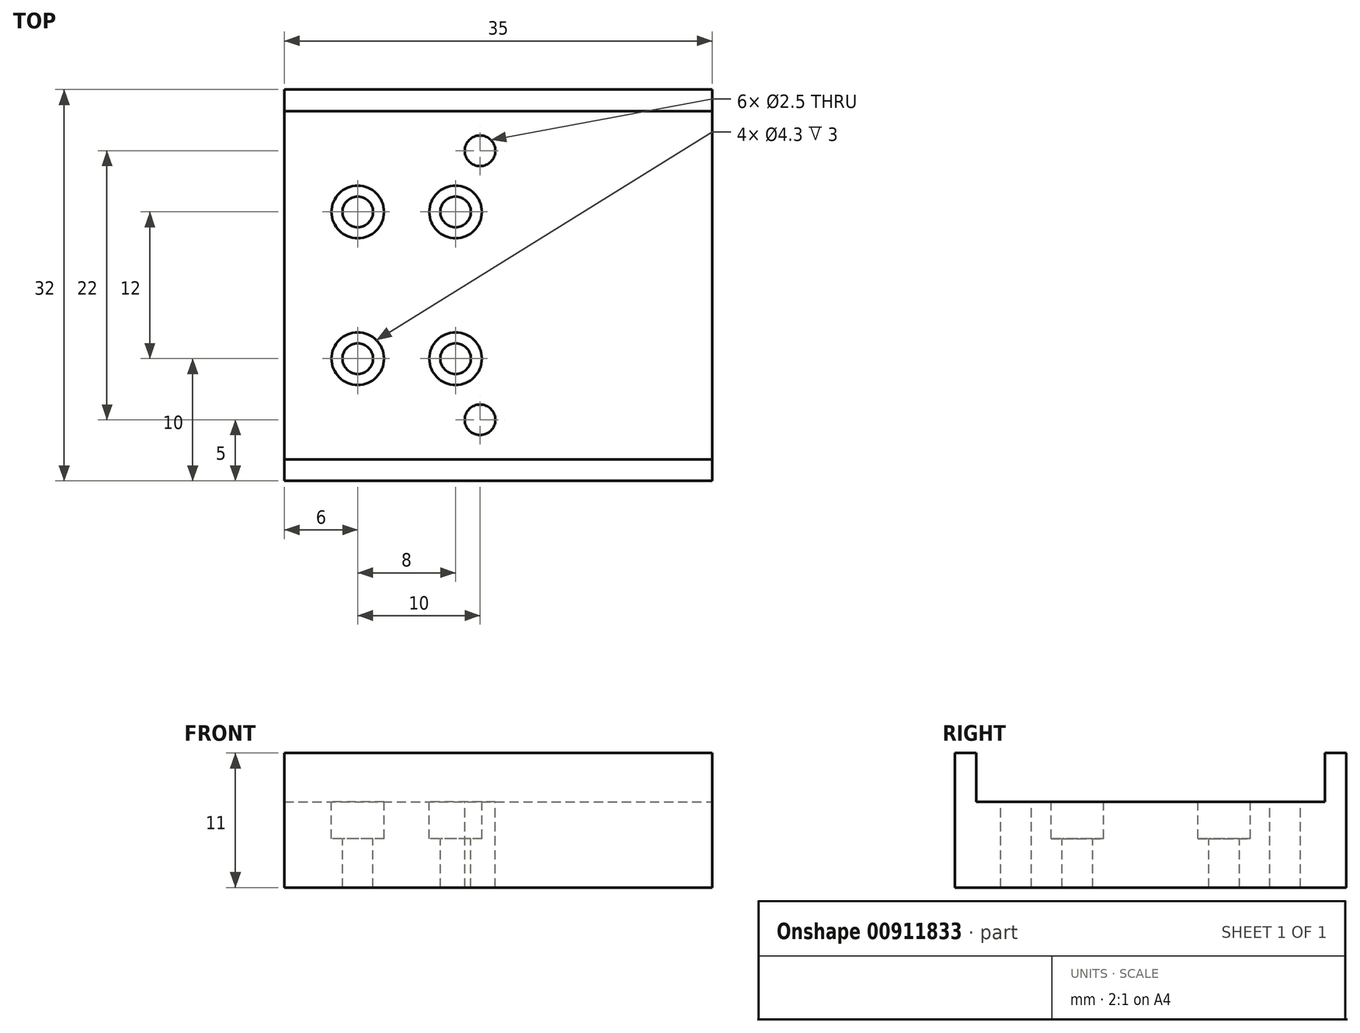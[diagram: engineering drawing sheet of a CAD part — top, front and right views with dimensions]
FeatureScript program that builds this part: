
annotation { "Feature Type Name" : "Feature", "Feature Type Description" : "" }
export const myFeature = defineFeature(function(context is Context, id is Id, definition is map)
    precondition{}
    {
        {
            var Q0;
            Q0=qCreatedBy(makeId("Top.planeOp"),FACE);
            var sketch = newSketch(context, id + "F0", { "sketchPlane" : qUnion([Q0])});
            skLineSegment(sketch, "E0.bottom", {"start": v(0, 0) * mm, "end": v(35, 0) * mm});
            skLineSegment(sketch, "E0.top", {"start": v(0, 32) * mm, "end": v(35, 32) * mm});
            skLineSegment(sketch, "E0.left", {"start": v(0, 0) * mm, "end": v(0, 32) * mm});
            skLineSegment(sketch, "E0.right", {"start": v(35, 0) * mm, "end": v(35, 32) * mm});
            skSolve(sketch);
        }
        {
            var Q0;
            Q0 = qSketchRegion(id + "F0", true);
            extrude(context, id + "F1", {"entities" : qUnion([Q0]), "depth" : 11 * mm, "offsetDistance" : 25 * mm});
        }
        {
            var Q0;
            Q0=makeQuery(id+"F1.opExtrude","CAP_FACE",FACE,{"disambiguationData":[OSD([sQuery(id+"F0.wireOp",EDGE,"E0.bottom"),sQuery(id+"F0.wireOp",EDGE,"E0.top"),sQuery(id+"F0.wireOp",EDGE,"E0.left"),sQuery(id+"F0.wireOp",EDGE,"E0.right")])],"isStart":false});
            var sketch = newSketch(context, id + "F2", { "sketchPlane" : qUnion([Q0])});
            skLineSegment(sketch, "E1.bottom", {"start": v(0, 30.25) * mm, "end": v(35, 30.25) * mm});
            skLineSegment(sketch, "E1.top", {"start": v(0, 1.75) * mm, "end": v(35, 1.75) * mm});
            skLineSegment(sketch, "E1.left", {"start": v(0, 30.25) * mm, "end": v(0, 1.75) * mm});
            skLineSegment(sketch, "E1.right", {"start": v(35, 30.25) * mm, "end": v(35, 1.75) * mm});
            skPoint(sketch, "E2", {"position": v(35, 16) * mm});
            skSolve(sketch);
        }
        {
            var Q0;
            Q0 = qSketchRegion(id + "F2", true);
            extrude(context, id + "F3", {"entities" : qUnion([Q0]), "operationType" : NewBodyOperationType.REMOVE, "oppositeDirection" : true, "depth" : 4 * mm, "offsetDistance" : 25 * mm});
        }
        {
            var Q0;
            Q0=makeQuery(id+"F3.boolean.opBoolean","COPY",FACE,{"derivedFrom":makeQuery(id+"F3.opExtrude","CAP_FACE",FACE,{"disambiguationData":[OSD([sQuery(id+"F2.wireOp",EDGE,"E1.bottom"),sQuery(id+"F2.wireOp",EDGE,"E1.top"),sQuery(id+"F2.wireOp",EDGE,"E1.left"),sQuery(id+"F2.wireOp",EDGE,"E1.right")])],"isStart":false})});
            var sketch = newSketch(context, id + "F4", { "sketchPlane" : qUnion([Q0])});
            skLineSegment(sketch, "E3", {"start": v(0, 16) * mm, "end": v(35, 16) * mm, "construction": true});
            skLineSegment(sketch, "E4", {"start": v(6, 25.01) * mm, "end": v(6, 7.08) * mm, "construction": true});
            skCircle(sketch, "E5", {"center": v(6, 22) * mm, "radius": 1.25 * mm});
            skCircle(sketch, "E6.0.1.0", {"center": v(6, 10) * mm, "radius": 1.25 * mm});
            skCircle(sketch, "E6.1.0.0", {"center": v(14, 22) * mm, "radius": 1.25 * mm});
            skCircle(sketch, "E6.1.1.0", {"center": v(14, 10) * mm, "radius": 1.25 * mm});
            skLineSegment(sketch, "E6.direction1", {"start": v(6, 22) * mm, "end": v(14, 22) * mm, "construction": true});
            skLineSegment(sketch, "E6.direction2", {"start": v(6, 22) * mm, "end": v(6, 10) * mm, "construction": true});
            skLineSegment(sketch, "E7", {"start": v(16, -1.34) * mm, "end": v(16, 34.49) * mm, "construction": true});
            skCircle(sketch, "E8", {"center": v(16, 27) * mm, "radius": 1.25 * mm});
            skCircle(sketch, "E9", {"center": v(16, 5) * mm, "radius": 1.25 * mm});
            skSolve(sketch);
        }
        {
            var Q0;
            Q0 = qSketchRegion(id + "F4", true);
            extrude(context, id + "F5", {"entities" : qUnion([Q0]), "operationType" : NewBodyOperationType.REMOVE, "oppositeDirection" : true, "depth" : 25 * mm, "offsetDistance" : 25 * mm});
        }
        {
            var Q0;
            Q0=makeQuery(id+"F3.boolean.opBoolean","COPY",FACE,{"derivedFrom":makeQuery(id+"F3.opExtrude","CAP_FACE",FACE,{"disambiguationData":[OSD([sQuery(id+"F2.wireOp",EDGE,"E1.bottom"),sQuery(id+"F2.wireOp",EDGE,"E1.top"),sQuery(id+"F2.wireOp",EDGE,"E1.left"),sQuery(id+"F2.wireOp",EDGE,"E1.right")])],"isStart":false})});
            var sketch = newSketch(context, id + "F6", { "sketchPlane" : qUnion([Q0])});
            skCircle(sketch, "E10", {"center": v(6, 22) * mm, "radius": 2.15 * mm});
            skCircle(sketch, "E11", {"center": v(14, 22) * mm, "radius": 2.15 * mm});
            skCircle(sketch, "E12", {"center": v(14, 10) * mm, "radius": 2.15 * mm});
            skCircle(sketch, "E13", {"center": v(6, 10) * mm, "radius": 2.15 * mm});
            skSolve(sketch);
        }
        {
            var Q0;
            Q0 = qSketchRegion(id + "F6", true);
            extrude(context, id + "F7", {"entities" : qUnion([Q0]), "operationType" : NewBodyOperationType.REMOVE, "oppositeDirection" : true, "depth" : 3 * mm, "offsetDistance" : 25 * mm});
        }
    });
